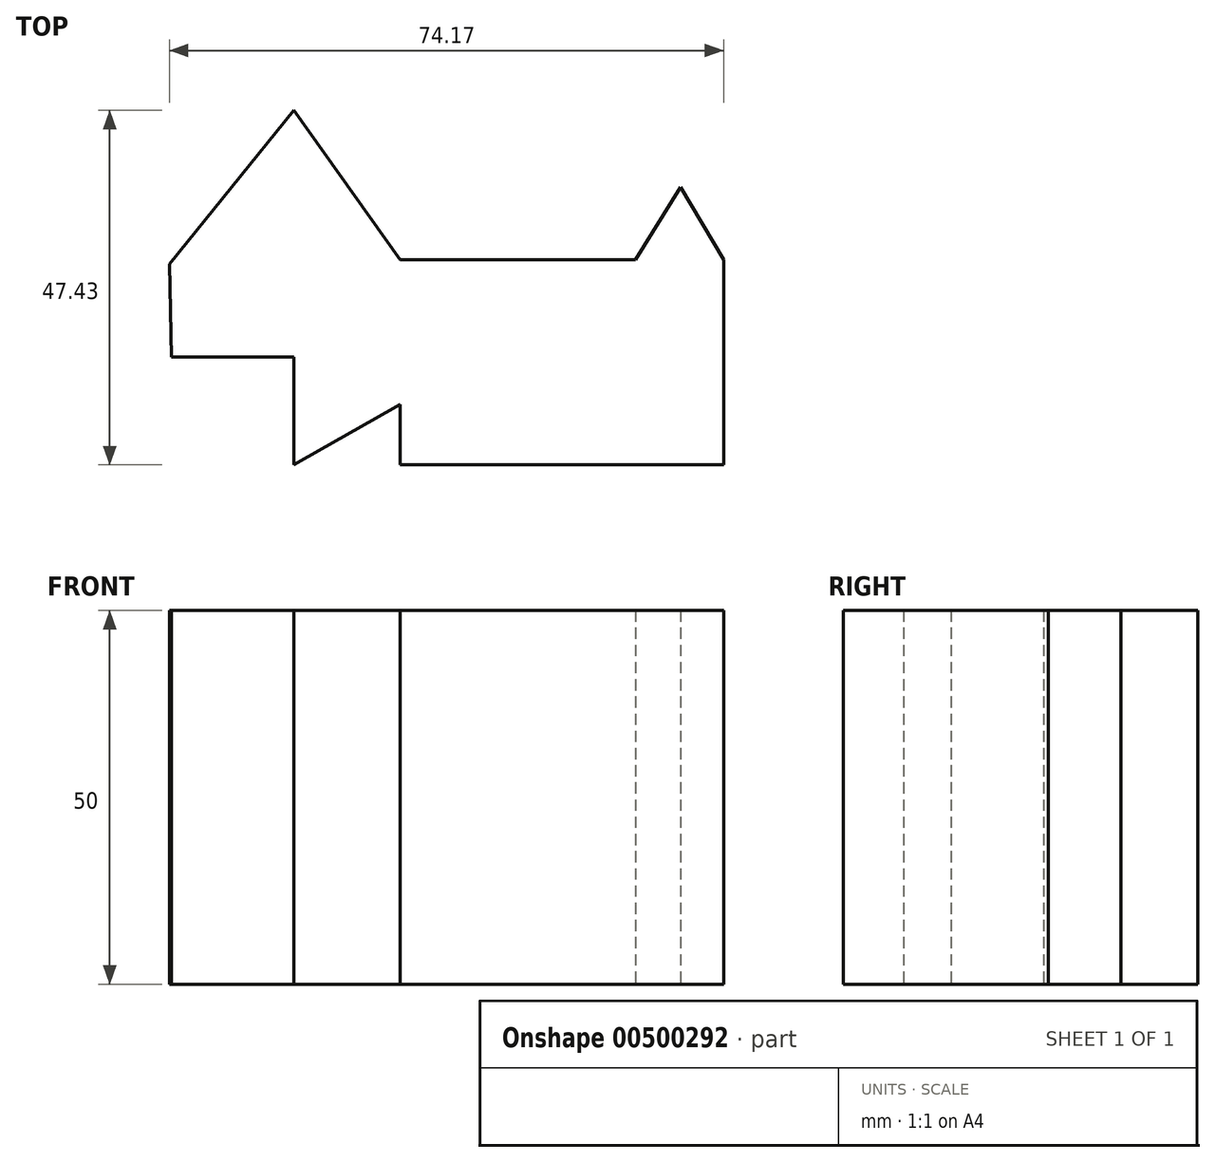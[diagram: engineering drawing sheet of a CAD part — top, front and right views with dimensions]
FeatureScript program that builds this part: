
annotation { "Feature Type Name" : "Feature", "Feature Type Description" : "" }
export const myFeature = defineFeature(function(context is Context, id is Id, definition is map)
    precondition{}
    {
        {
            var Q0;
            Q0=qCreatedBy(makeId("Top.planeOp"),FACE);
            var sketch = newSketch(context, id + "F0", { "sketchPlane" : qUnion([Q0])});
            skLineSegment(sketch, "E0", {"start": v(-57.04, 26.84) * mm, "end": v(-40.4, 47.43) * mm});
            skLineSegment(sketch, "E1", {"start": v(-40.4, 47.43) * mm, "end": v(-26.17, 27.45) * mm});
            skLineSegment(sketch, "E2", {"start": v(-26.17, 27.45) * mm, "end": v(5.32, 27.45) * mm});
            skLineSegment(sketch, "E3", {"start": v(5.32, 27.45) * mm, "end": v(11.37, 37.14) * mm});
            skLineSegment(sketch, "E4", {"start": v(11.37, 37.14) * mm, "end": v(17.13, 27.45) * mm});
            skLineSegment(sketch, "E5", {"start": v(17.13, 27.45) * mm, "end": v(17.13, 0) * mm});
            skLineSegment(sketch, "E6", {"start": v(17.13, 0) * mm, "end": v(-26.17, 0) * mm});
            skLineSegment(sketch, "E7", {"start": v(-26.17, 0) * mm, "end": v(-26.17, 8.07) * mm});
            skLineSegment(sketch, "E8", {"start": v(-26.17, 8.07) * mm, "end": v(-40.4, 0) * mm});
            skLineSegment(sketch, "E9", {"start": v(-40.4, 0) * mm, "end": v(-40.4, 14.43) * mm});
            skLineSegment(sketch, "E10", {"start": v(-40.4, 14.43) * mm, "end": v(-56.74, 14.43) * mm});
            skLineSegment(sketch, "E11", {"start": v(-56.74, 14.43) * mm, "end": v(-57.04, 26.84) * mm});
            skSolve(sketch);
        }
        {
            var Q0;
            Q0=makeQuery(id+"F0.imprint","IMPRINT",FACE,{"disambiguationData":[TD([[makeQuery(id+"F0.imprint","IMPRINT",EDGE,{"derivedFrom":sQuery(id+"F0.wireOp",EDGE,"E0")}),-1.0]])]});
            extrude(context, id + "F1", {"entities" : qUnion([Q0]), "depth" : 50 * mm});
        }
    });
